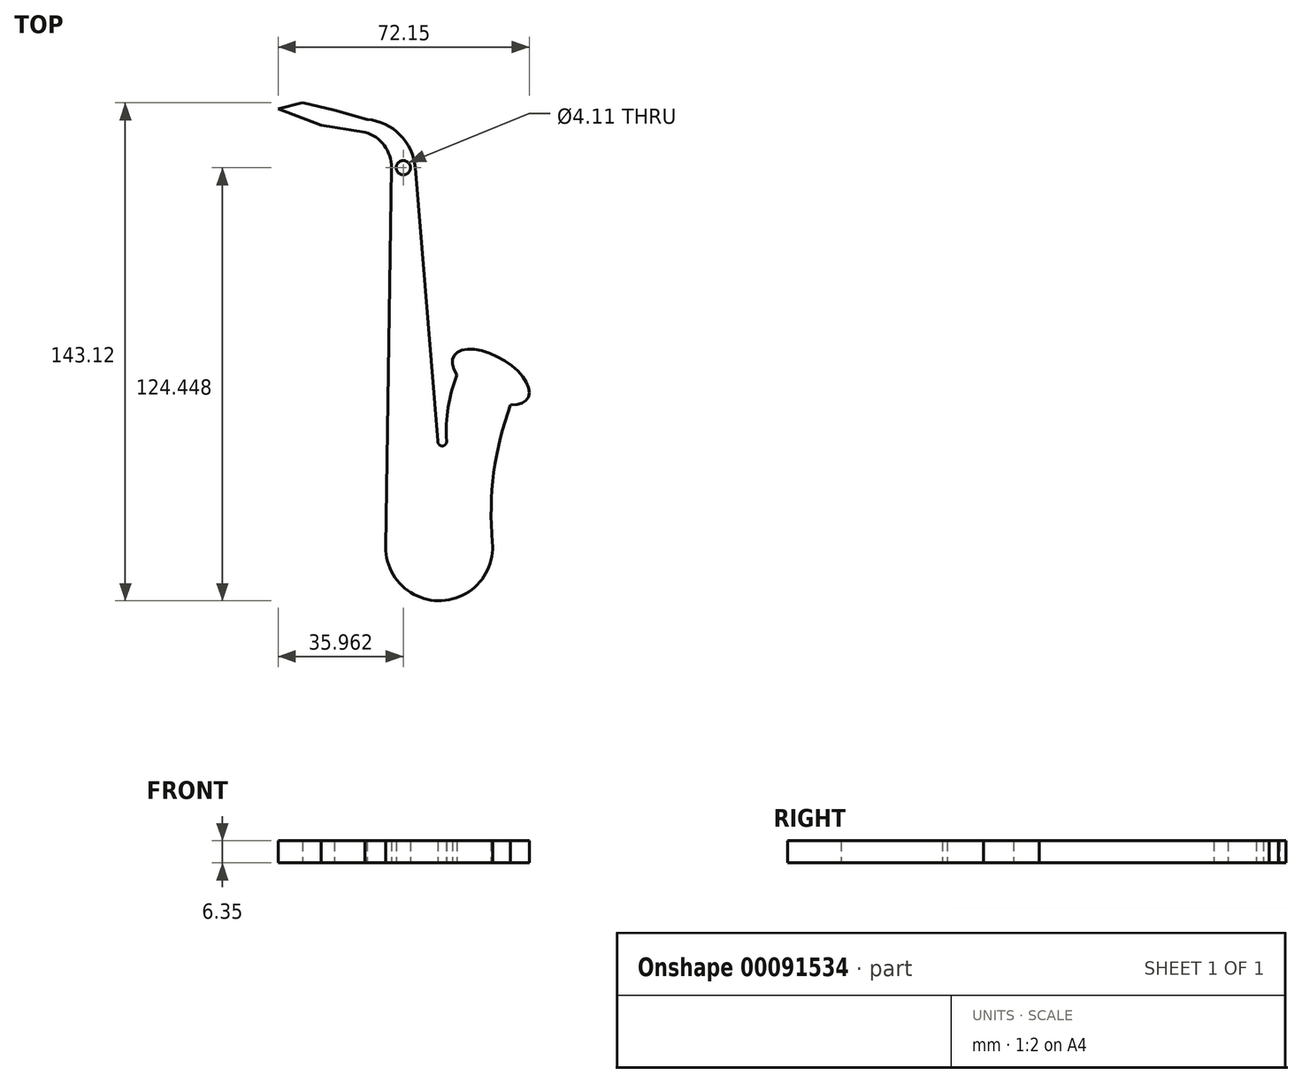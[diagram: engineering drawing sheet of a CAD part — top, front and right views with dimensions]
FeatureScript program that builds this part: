
annotation { "Feature Type Name" : "Feature", "Feature Type Description" : "" }
export const myFeature = defineFeature(function(context is Context, id is Id, definition is map)
    precondition{}
    {
        {
            var Q0;
            Q0=qCreatedBy(makeId("Top.planeOp"),FACE);
            var sketch = newSketch(context, id + "F0", { "sketchPlane" : qUnion([Q0])});
            skEllipse(sketch, "E0", {"center": v(26.2, -9.68) * mm, "majorRadius": 12.23 * mm, "minorRadius": 6.06 * mm, "majorAxis": v(0.87, -0.5)});
            skArc(sketch, "E1", {"start": v(-4.01, -58.54) * mm, "mid": v(12.07, -73.93) * mm, "end": v(26.67, -57.13) * mm});
            skArc(sketch, "E2", {"start": v(31.88, -17.69) * mm, "mid": v(27.06, -37.12) * mm, "end": v(26.67, -57.13) * mm});
            skLineSegment(sketch, "E3", {"start": v(-4.01, -58.54) * mm, "end": v(-2.36, 50.5) * mm});
            skLineSegment(sketch, "E4", {"start": v(0, 0) * mm, "end": v(-3.13, 0) * mm});
            skLineSegment(sketch, "E5", {"start": v(0, 0) * mm, "end": v(11.36, -58.57) * mm});
            skLineSegment(sketch, "E6", {"start": v(11.36, -58.57) * mm, "end": v(115.85, -48.85) * mm, "construction": true});
            skArc(sketch, "E7", {"start": v(16.48, -9.01) * mm, "mid": v(13.95, -18.38) * mm, "end": v(13.5, -28.07) * mm});
            skLineSegment(sketch, "E8", {"start": v(11.36, -58.57) * mm, "end": v(57.94, -25.27) * mm, "construction": true});
            skArc(sketch, "E9", {"start": v(11, -28.07) * mm, "mid": v(12.24, -29.46) * mm, "end": v(13.5, -28.07) * mm});
            skLineSegment(sketch, "E10", {"start": v(12.24, -28.2) * mm, "end": v(11.36, -58.57) * mm});
            skLineSegment(sketch, "E11", {"start": v(11, -28.07) * mm, "end": v(4.48, 50.5) * mm});
            skArc(sketch, "E12", {"start": v(-2.36, 50.5) * mm, "mid": v(-4.41, 56.9) * mm, "end": v(-9.91, 60.74) * mm});
            skLineSegment(sketch, "E13", {"start": v(-9.91, 60.74) * mm, "end": v(-22.54, 62.74) * mm});
            skLineSegment(sketch, "E14", {"start": v(-2.36, 50.5) * mm, "end": v(-12.85, 50.67) * mm, "construction": true});
            skLineSegment(sketch, "E15", {"start": v(-9.91, 60.74) * mm, "end": v(-9.34, 64.36) * mm});
            skArc(sketch, "E16", {"start": v(4.48, 50.5) * mm, "mid": v(0.1, 59.96) * mm, "end": v(-9.34, 64.36) * mm});
            skLineSegment(sketch, "E17", {"start": v(-22.54, 62.74) * mm, "end": v(-34.9, 67.4) * mm});
            skLineSegment(sketch, "E18", {"start": v(-34.9, 67.4) * mm, "end": v(-27.88, 69.18) * mm});
            skLineSegment(sketch, "E19", {"start": v(-27.88, 69.18) * mm, "end": v(-18.76, 67.08) * mm});
            skLineSegment(sketch, "E20", {"start": v(-18.76, 67.08) * mm, "end": v(-9.34, 64.36) * mm});
            skLineSegment(sketch, "E21", {"start": v(-2.36, 50.5) * mm, "end": v(4.48, 50.5) * mm});
            skCircle(sketch, "E22", {"center": v(1.06, 50.5) * mm, "radius": 2.05 * mm});
            skSolve(sketch);
        }
        {
            var Q0;
            Q0 = qSketchRegion(id + "F0", true);
            var Q1;
            Q1=sQuery(id+"F0.wireOp",EDGE,"E14");
            extrude(context, id + "F1", {"entities" : qUnion([Q0]), "surfaceEntities" : qUnion([Q1]), "depth" : 6.35 * mm});
        }
    });
